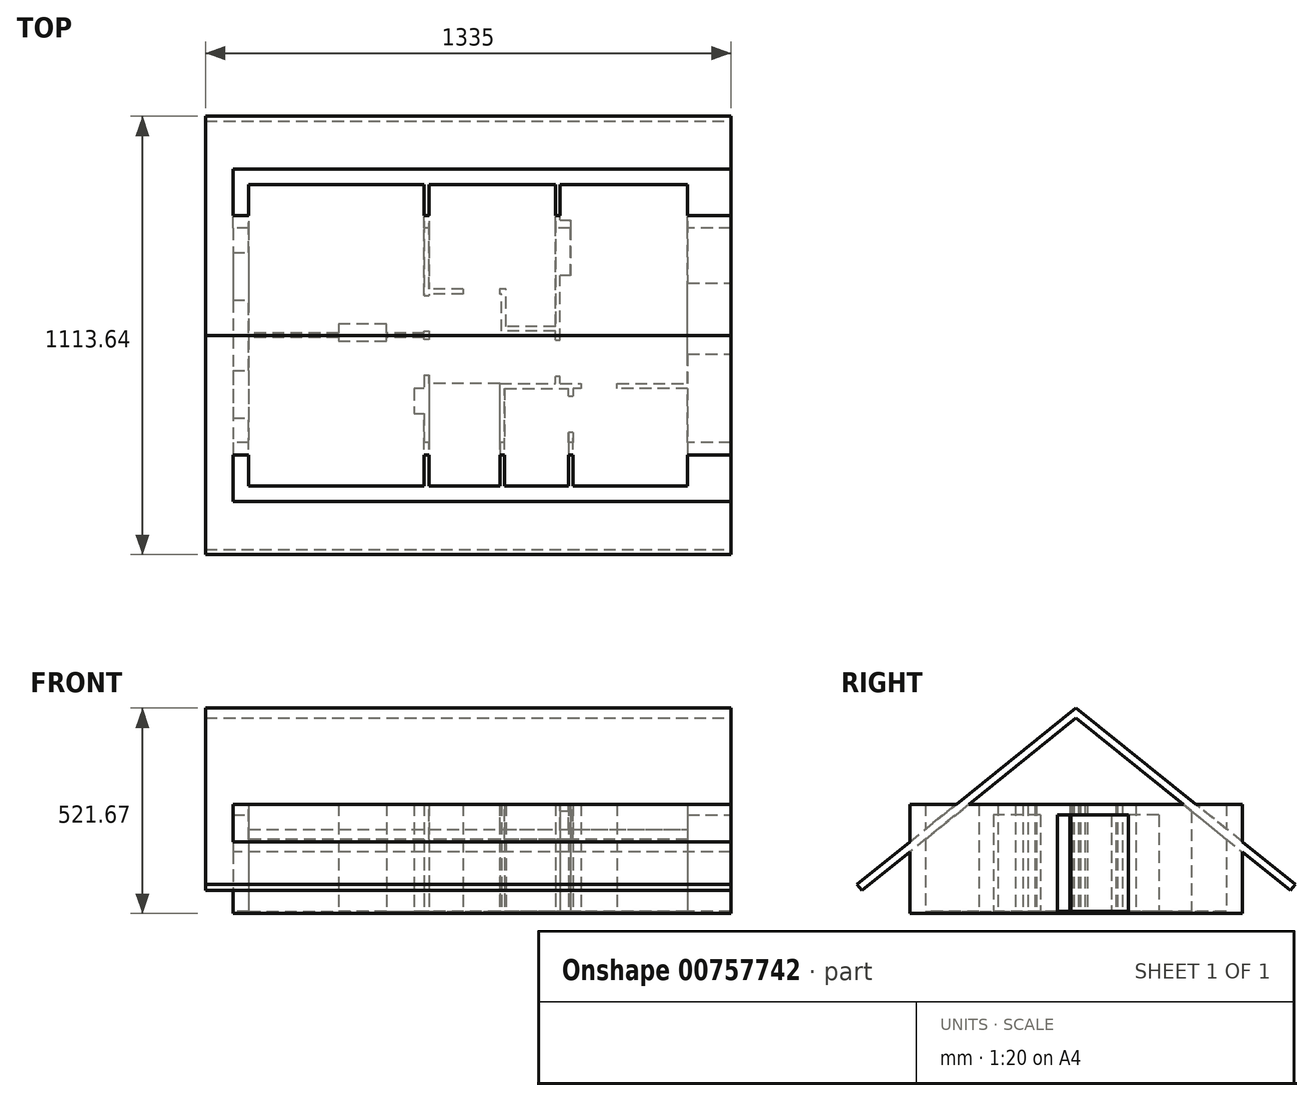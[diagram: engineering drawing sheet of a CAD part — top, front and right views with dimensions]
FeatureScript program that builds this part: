
annotation { "Feature Type Name" : "Feature", "Feature Type Description" : "" }
export const myFeature = defineFeature(function(context is Context, id is Id, definition is map)
    precondition{}
    {
        {
            var Q0;
            Q0=qCreatedBy(makeId("Top.planeOp"),FACE);
            var sketch = newSketch(context, id + "F0", { "sketchPlane" : qUnion([Q0])});
            skLineSegment(sketch, "E0", {"start": v(0, 0) * mm, "end": v(1145, 0) * mm, "construction": true});
            skLineSegment(sketch, "E1", {"start": v(1145, 0) * mm, "end": v(1145, 795) * mm, "construction": true});
            skLineSegment(sketch, "E2", {"start": v(1145, 795) * mm, "end": v(0, 795) * mm, "construction": true});
            skLineSegment(sketch, "E3", {"start": v(0, 795) * mm, "end": v(0, 0) * mm, "construction": true});
            skLineSegment(sketch, "E4", {"start": v(800, 0) * mm, "end": v(800, 15) * mm, "construction": true});
            skLineSegment(sketch, "E5", {"start": v(800, 397.5) * mm, "end": v(0, 397.5) * mm, "construction": true});
            skLineSegment(sketch, "E6.0", {"start": v(1170, 820) * mm, "end": v(-25, 820) * mm});
            skLineSegment(sketch, "E6.1", {"start": v(1170, -25) * mm, "end": v(1170, 820) * mm});
            skLineSegment(sketch, "E6.2", {"start": v(-25, -25) * mm, "end": v(1170, -25) * mm});
            skLineSegment(sketch, "E6.3", {"start": v(-25, 820) * mm, "end": v(-25, -25) * mm});
            skLineSegment(sketch, "E7.0", {"start": v(1130, 780) * mm, "end": v(15, 780) * mm});
            skLineSegment(sketch, "E7.1", {"start": v(1130, 15) * mm, "end": v(1130, 780) * mm});
            skLineSegment(sketch, "E7.2", {"start": v(15, 15) * mm, "end": v(1130, 15) * mm});
            skLineSegment(sketch, "E7.3", {"start": v(15, 780) * mm, "end": v(15, 15) * mm});
            skLineSegment(sketch, "E8.0", {"start": v(806, 263) * mm, "end": v(806, 795) * mm});
            skLineSegment(sketch, "E9.0", {"start": v(794, 263) * mm, "end": v(794, 795) * mm});
            skLineSegment(sketch, "E10", {"start": v(461, 386.5) * mm, "end": v(461, 262.5) * mm});
            skLineSegment(sketch, "E11", {"start": v(461, 262.5) * mm, "end": v(435, 262.5) * mm});
            skLineSegment(sketch, "E12", {"start": v(435, 262.5) * mm, "end": v(435, 198.5) * mm});
            skLineSegment(sketch, "E13", {"start": v(435, 198.5) * mm, "end": v(461, 198.5) * mm});
            skLineSegment(sketch, "E14", {"start": v(461, 198.5) * mm, "end": v(461, 15) * mm});
            skLineSegment(sketch, "E15", {"start": v(806, 691) * mm, "end": v(832, 691) * mm});
            skLineSegment(sketch, "E16", {"start": v(832, 691) * mm, "end": v(832, 549) * mm});
            skLineSegment(sketch, "E17", {"start": v(832, 549) * mm, "end": v(806, 549) * mm});
            skLineSegment(sketch, "E18", {"start": v(365, 426.5) * mm, "end": v(243, 426.5) * mm});
            skLineSegment(sketch, "E19", {"start": v(323, 15) * mm, "end": v(323, -25) * mm});
            skLineSegment(sketch, "E20", {"start": v(461, 15) * mm, "end": v(461, -25) * mm});
            skLineSegment(sketch, "E21", {"start": v(1130, 530) * mm, "end": v(1170, 530) * mm});
            skLineSegment(sketch, "E22", {"start": v(1130, 350) * mm, "end": v(1170, 350) * mm});
            skPoint(sketch, "E23.orphan", {"position": v(238, -25) * mm});
            skPoint(sketch, "E24.end.orphan", {"position": v(88, -25) * mm});
            skLineSegment(sketch, "E25", {"start": v(-25, 487.5) * mm, "end": v(15, 487.5) * mm});
            skLineSegment(sketch, "E26", {"start": v(-25, 607.5) * mm, "end": v(15, 607.5) * mm});
            skLineSegment(sketch, "E27", {"start": v(-25, 307.5) * mm, "end": v(15, 307.5) * mm});
            skLineSegment(sketch, "E28", {"start": v(-25, 187.5) * mm, "end": v(15, 187.5) * mm});
            skLineSegment(sketch, "E29", {"start": v(794, 408) * mm, "end": v(657, 408) * mm});
            skLineSegment(sketch, "E30", {"start": v(657, 408) * mm, "end": v(657, 503) * mm});
            skLineSegment(sketch, "E31", {"start": v(657, 503) * mm, "end": v(473, 503) * mm});
            skLineSegment(sketch, "E32.0", {"start": v(669, 515) * mm, "end": v(473, 515) * mm});
            skLineSegment(sketch, "E32.1", {"start": v(669, 420) * mm, "end": v(669, 515) * mm});
            skLineSegment(sketch, "E32.2", {"start": v(794, 420) * mm, "end": v(669, 420) * mm});
            skLineSegment(sketch, "E33", {"start": v(652, 515) * mm, "end": v(652, 503) * mm});
            skLineSegment(sketch, "E34", {"start": v(560, 515) * mm, "end": v(560, 503) * mm});
            skLineSegment(sketch, "E35", {"start": v(461, 403.5) * mm, "end": v(365, 403.5) * mm});
            skLineSegment(sketch, "E36", {"start": v(365, 403.5) * mm, "end": v(15, 403.5) * mm});
            skLineSegment(sketch, "E37", {"start": v(15, 403.5) * mm, "end": v(15, 382.16) * mm});
            skLineSegment(sketch, "E38", {"start": v(794, 385) * mm, "end": v(806, 385) * mm});
            skLineSegment(sketch, "E39", {"start": v(806, 385) * mm, "end": v(806, 293) * mm});
            skLineSegment(sketch, "E40", {"start": v(806, 293) * mm, "end": v(794, 293) * mm});
            skLineSegment(sketch, "E41.MirrorCS", {"start": v(461, 391.5) * mm, "end": v(365, 391.5) * mm});
            skLineSegment(sketch, "E42.MirrorCS", {"start": v(365, 391.5) * mm, "end": v(15, 391.5) * mm});
            skLineSegment(sketch, "E43", {"start": v(461, 403.5) * mm, "end": v(461, 408.5) * mm});
            skLineSegment(sketch, "E44", {"start": v(461, 408.5) * mm, "end": v(473, 408.5) * mm});
            skLineSegment(sketch, "E45", {"start": v(473, 408.5) * mm, "end": v(473, 386.5) * mm});
            skLineSegment(sketch, "E46", {"start": v(473, 386.5) * mm, "end": v(461, 386.5) * mm});
            skLineSegment(sketch, "E47", {"start": v(461, 386.5) * mm, "end": v(461, 391.5) * mm});
            skLineSegment(sketch, "E48", {"start": v(243, 426.5) * mm, "end": v(243, 382.5) * mm});
            skLineSegment(sketch, "E49", {"start": v(243, 382.5) * mm, "end": v(364.87, 382.5) * mm});
            skLineSegment(sketch, "E50", {"start": v(364.87, 382.5) * mm, "end": v(365, 426.5) * mm});
            skLineSegment(sketch, "E51", {"start": v(461, 408.5) * mm, "end": v(461, 780) * mm});
            skLineSegment(sketch, "E52", {"start": v(461, 780) * mm, "end": v(473, 780) * mm});
            skLineSegment(sketch, "E53", {"start": v(473, 780) * mm, "end": v(473, 408.5) * mm});
            skLineSegment(sketch, "E54", {"start": v(461, 498.5) * mm, "end": v(473, 498.5) * mm});
            skLineSegment(sketch, "E55", {"start": v(473, 386.5) * mm, "end": v(473, 15) * mm});
            skLineSegment(sketch, "E56", {"start": v(461, 296.5) * mm, "end": v(473, 296.5) * mm});
            skLineSegment(sketch, "E57", {"start": v(653, 15) * mm, "end": v(653, 275) * mm});
            skLineSegment(sketch, "E58", {"start": v(653, 275) * mm, "end": v(670, 275) * mm});
            skLineSegment(sketch, "E59", {"start": v(665, 263) * mm, "end": v(665, 15) * mm});
            skLineSegment(sketch, "E60", {"start": v(653, 275) * mm, "end": v(473, 275) * mm});
            skLineSegment(sketch, "E61", {"start": v(670, 275) * mm, "end": v(794, 275) * mm});
            skLineSegment(sketch, "E62", {"start": v(794, 275) * mm, "end": v(794, 263) * mm});
            skLineSegment(sketch, "E63", {"start": v(665, 263) * mm, "end": v(794, 263) * mm});
            skLineSegment(sketch, "E64", {"start": v(794, 275) * mm, "end": v(839, 275) * mm});
            skLineSegment(sketch, "E65", {"start": v(839, 275) * mm, "end": v(839, 15) * mm});
            skLineSegment(sketch, "E66", {"start": v(839, 15) * mm, "end": v(827, 15) * mm});
            skLineSegment(sketch, "E67", {"start": v(827, 15) * mm, "end": v(827, 263) * mm});
            skLineSegment(sketch, "E68", {"start": v(827, 263) * mm, "end": v(794, 263) * mm});
            skLineSegment(sketch, "E69", {"start": v(839, 275) * mm, "end": v(1130, 275) * mm});
            skLineSegment(sketch, "E70", {"start": v(1130, 275) * mm, "end": v(1130, 263) * mm});
            skLineSegment(sketch, "E71", {"start": v(1130, 263) * mm, "end": v(827, 263) * mm});
            skLineSegment(sketch, "E72.trimOffspring", {"start": v(800, 263) * mm, "end": v(800, 795) * mm, "construction": true});
            skLineSegment(sketch, "E73", {"start": v(827, 243) * mm, "end": v(839, 243) * mm});
            skLineSegment(sketch, "E74", {"start": v(839, 243) * mm, "end": v(839, 151) * mm});
            skLineSegment(sketch, "E75", {"start": v(839, 151) * mm, "end": v(827, 151) * mm});
            skLineSegment(sketch, "E76", {"start": v(859, 275) * mm, "end": v(859, 263) * mm});
            skLineSegment(sketch, "E77", {"start": v(859, 263) * mm, "end": v(951, 263) * mm});
            skLineSegment(sketch, "E78", {"start": v(951, 263) * mm, "end": v(951, 275) * mm});
            skSolve(sketch);
        }
        {
            var Q0;
            {var subQ5=sQuery(id+"F0.wireOp",EDGE,"E78");Q0=makeQuery(id+"F0.imprint","IMPRINT",FACE,{"disambiguationData":[TD([[makeQuery(id+"F0.imprint","IMPRINT",EDGE,{"derivedFrom":subQ5}),-1.0]])]});}
            var Q1;
            {var subQ3=sQuery(id+"F0.wireOp",EDGE,"E29");Q1=makeQuery(id+"F0.imprint","IMPRINT",FACE,{"disambiguationData":[TD([[makeQuery(id+"F0.imprint","IMPRINT",EDGE,{"derivedFrom":subQ3}),-1.0]])]});}
            var Q2;
            {var subQ2=sQuery(id+"F0.wireOp",EDGE,"E19");Q2=makeQuery(id+"F0.imprint","IMPRINT",FACE,{"disambiguationData":[TD([[makeQuery(id+"F0.imprint","IMPRINT",EDGE,{"derivedFrom":subQ2}),1.0]])]});}
            var Q3;
            {var subQ0=sQuery(id+"F0.wireOp",EDGE,"E15");Q3=makeQuery(id+"F0.imprint","IMPRINT",FACE,{"disambiguationData":[TD([[makeQuery(id+"F0.imprint","IMPRINT",EDGE,{"derivedFrom":subQ0}),1.0]])]});}
            var Q4;
            {var subQ0=sQuery(id+"F0.wireOp",EDGE,"E25");Q4=makeQuery(id+"F0.imprint","IMPRINT",FACE,{"disambiguationData":[TD([[makeQuery(id+"F0.imprint","IMPRINT",EDGE,{"derivedFrom":subQ0}),1.0]])]});}
            var Q5;
            {var subQ0=sQuery(id+"F0.wireOp",EDGE,"E27");Q5=makeQuery(id+"F0.imprint","IMPRINT",FACE,{"disambiguationData":[TD([[makeQuery(id+"F0.imprint","IMPRINT",EDGE,{"derivedFrom":subQ0}),-1.0]])]});}
            var Q6;
            {var subQ5=sQuery(id+"F0.wireOp",EDGE,"E25");Q6=makeQuery(id+"F0.imprint","IMPRINT",FACE,{"disambiguationData":[TD([[makeQuery(id+"F0.imprint","IMPRINT",EDGE,{"derivedFrom":subQ5}),-1.0]])]});}
            var Q7;
            {var subQ4=sQuery(id+"F0.wireOp",EDGE,"E19");Q7=makeQuery(id+"F0.imprint","IMPRINT",FACE,{"disambiguationData":[TD([[makeQuery(id+"F0.imprint","IMPRINT",EDGE,{"derivedFrom":subQ4}),-1.0]])]});}
            var Q8;
            {var subQ4=sQuery(id+"F0.wireOp",EDGE,"E7.1");var subQ7=sQuery(id+"F0.wireOp",EDGE,"E71");var subQ8=makeQuery(id+"F0.imprint","INTERSECT",VERTEX,{"derivedFrom":[subQ4,subQ7]});Q8=makeQuery(id+"F0.imprint","IMPRINT",FACE,{"disambiguationData":[TD([[makeQuery(id+"F0.imprint","IMPRINT",EDGE,{"disambiguationData":[TD([[subQ8,1.0]])],"derivedFrom":subQ4}),1.0]])]});}
            var Q9;
            {var subQ2=sQuery(id+"F0.wireOp",EDGE,"E76");Q9=makeQuery(id+"F0.imprint","IMPRINT",FACE,{"disambiguationData":[TD([[makeQuery(id+"F0.imprint","IMPRINT",EDGE,{"derivedFrom":subQ2}),1.0]])]});}
            var Q10;
            {var subQ5=sQuery(id+"F0.wireOp",EDGE,"E49");Q10=makeQuery(id+"F0.imprint","IMPRINT",FACE,{"disambiguationData":[TD([[makeQuery(id+"F0.imprint","IMPRINT",EDGE,{"derivedFrom":subQ5}),1.0]])]});}
            var Q11;
            {var subQ6=sQuery(id+"F0.wireOp",EDGE,"E54");Q11=makeQuery(id+"F0.imprint","IMPRINT",FACE,{"disambiguationData":[TD([[makeQuery(id+"F0.imprint","IMPRINT",EDGE,{"derivedFrom":subQ6}),1.0]])]});}
            var Q12;
            {var subQ0=sQuery(id+"F0.wireOp",EDGE,"E44");Q12=makeQuery(id+"F0.imprint","IMPRINT",FACE,{"disambiguationData":[TD([[makeQuery(id+"F0.imprint","IMPRINT",EDGE,{"derivedFrom":subQ0}),1.0]])]});}
            var Q13;
            {var subQ0=sQuery(id+"F0.wireOp",EDGE,"E18");Q13=makeQuery(id+"F0.imprint","IMPRINT",FACE,{"disambiguationData":[TD([[makeQuery(id+"F0.imprint","IMPRINT",EDGE,{"derivedFrom":subQ0}),1.0]])]});}
            var Q14;
            {var subQ9=sQuery(id+"F0.wireOp",EDGE,"E29");Q14=makeQuery(id+"F0.imprint","IMPRINT",FACE,{"disambiguationData":[TD([[makeQuery(id+"F0.imprint","IMPRINT",EDGE,{"derivedFrom":subQ9}),1.0]])]});}
            var Q15;
            {var subQ0=sQuery(id+"F0.wireOp",EDGE,"E21");Q15=makeQuery(id+"F0.imprint","IMPRINT",FACE,{"disambiguationData":[TD([[makeQuery(id+"F0.imprint","IMPRINT",EDGE,{"derivedFrom":subQ0}),-1.0]])]});}
            var Q16;
            {var subQ7=sQuery(id+"F0.wireOp",EDGE,"E59");Q16=makeQuery(id+"F0.imprint","IMPRINT",FACE,{"disambiguationData":[TD([[makeQuery(id+"F0.imprint","IMPRINT",EDGE,{"derivedFrom":subQ7}),1.0]])]});}
            var Q17;
            {var subQ0=sQuery(id+"F0.wireOp",EDGE,"E34");Q17=makeQuery(id+"F0.imprint","IMPRINT",FACE,{"disambiguationData":[TD([[makeQuery(id+"F0.imprint","IMPRINT",EDGE,{"derivedFrom":subQ0}),-1.0]])]});}
            var Q18;
            {var subQ0=sQuery(id+"F0.wireOp",EDGE,"E46");Q18=makeQuery(id+"F0.imprint","IMPRINT",FACE,{"disambiguationData":[TD([[makeQuery(id+"F0.imprint","IMPRINT",EDGE,{"derivedFrom":subQ0}),1.0]])]});}
            var Q19;
            {var subQ0=sQuery(id+"F0.wireOp",EDGE,"E11");Q19=makeQuery(id+"F0.imprint","IMPRINT",FACE,{"disambiguationData":[TD([[makeQuery(id+"F0.imprint","IMPRINT",EDGE,{"derivedFrom":subQ0}),-1.0]])]});}
            var Q20;
            {var subQ5=sQuery(id+"F0.wireOp",EDGE,"E6.0");Q20=makeQuery(id+"F0.imprint","IMPRINT",FACE,{"disambiguationData":[TD([[makeQuery(id+"F0.imprint","IMPRINT",EDGE,{"derivedFrom":subQ5}),1.0]])]});}
            var Q21;
            {var subQ2=sQuery(id+"F0.wireOp",EDGE,"E73");Q21=makeQuery(id+"F0.imprint","IMPRINT",FACE,{"disambiguationData":[TD([[makeQuery(id+"F0.imprint","IMPRINT",EDGE,{"derivedFrom":subQ2}),-1.0]])]});}
            var Q22;
            {var subQ0=sQuery(id+"F0.wireOp",EDGE,"E11");Q22=makeQuery(id+"F0.imprint","IMPRINT",FACE,{"disambiguationData":[TD([[makeQuery(id+"F0.imprint","IMPRINT",EDGE,{"derivedFrom":subQ0}),1.0]])]});}
            var Q23;
            {var subQ10=sQuery(id+"F0.wireOp",EDGE,"E32.1");Q23=makeQuery(id+"F0.imprint","IMPRINT",FACE,{"disambiguationData":[TD([[makeQuery(id+"F0.imprint","IMPRINT",EDGE,{"derivedFrom":subQ10}),-1.0]])]});}
            var Q24;
            {var subQ0=sQuery(id+"F0.wireOp",EDGE,"E15");Q24=makeQuery(id+"F0.imprint","IMPRINT",FACE,{"disambiguationData":[TD([[makeQuery(id+"F0.imprint","IMPRINT",EDGE,{"derivedFrom":subQ0}),-1.0]])]});}
            var Q25;
            {var subQ0=sQuery(id+"F0.wireOp",EDGE,"E33");Q25=makeQuery(id+"F0.imprint","IMPRINT",FACE,{"disambiguationData":[TD([[makeQuery(id+"F0.imprint","IMPRINT",EDGE,{"derivedFrom":subQ0}),-1.0]])]});}
            var Q26;
            {var subQ5=sQuery(id+"F0.wireOp",EDGE,"E75");Q26=makeQuery(id+"F0.imprint","IMPRINT",FACE,{"disambiguationData":[TD([[makeQuery(id+"F0.imprint","IMPRINT",EDGE,{"derivedFrom":subQ5}),1.0]])]});}
            var Q27;
            {var subQ3=sQuery(id+"F0.wireOp",EDGE,"E57");Q27=makeQuery(id+"F0.imprint","IMPRINT",FACE,{"disambiguationData":[TD([[makeQuery(id+"F0.imprint","IMPRINT",EDGE,{"derivedFrom":subQ3}),-1.0]])]});}
            var Q28;
            {var subQ8=sQuery(id+"F0.wireOp",EDGE,"E20");Q28=makeQuery(id+"F0.imprint","IMPRINT",FACE,{"disambiguationData":[TD([[makeQuery(id+"F0.imprint","IMPRINT",EDGE,{"derivedFrom":subQ8}),1.0]])]});}
            var Q29;
            {var subQ0=sQuery(id+"F0.wireOp",EDGE,"E38");Q29=makeQuery(id+"F0.imprint","IMPRINT",FACE,{"disambiguationData":[TD([[makeQuery(id+"F0.imprint","IMPRINT",EDGE,{"derivedFrom":subQ0}),-1.0]])]});}
            var Q30;
            {var subQ0=sQuery(id+"F0.wireOp",EDGE,"E36");var subQ1=sQuery(id+"F0.wireOp",EDGE,"E7.3");var subQ2=makeQuery(id+"F0.imprint","INTERSECT",VERTEX,{"derivedFrom":[subQ1,subQ0]});Q30=makeQuery(id+"F0.imprint","IMPRINT",FACE,{"disambiguationData":[TD([[makeQuery(id+"F0.imprint","IMPRINT",EDGE,{"disambiguationData":[TD([[subQ2,-1.0]])],"derivedFrom":subQ1}),1.0]])]});}
            var Q31;
            {var subQ3=sQuery(id+"F0.wireOp",EDGE,"E40");Q31=makeQuery(id+"F0.imprint","IMPRINT",FACE,{"disambiguationData":[TD([[makeQuery(id+"F0.imprint","IMPRINT",EDGE,{"derivedFrom":subQ3}),1.0]])]});}
            var Q32;
            {var subQ5=sQuery(id+"F0.wireOp",EDGE,"E38");Q32=makeQuery(id+"F0.imprint","IMPRINT",FACE,{"disambiguationData":[TD([[makeQuery(id+"F0.imprint","IMPRINT",EDGE,{"derivedFrom":subQ5}),1.0]])]});}
            var Q33;
            {var subQ3=sQuery(id+"F0.wireOp",EDGE,"E73");Q33=makeQuery(id+"F0.imprint","IMPRINT",FACE,{"disambiguationData":[TD([[makeQuery(id+"F0.imprint","IMPRINT",EDGE,{"derivedFrom":subQ3}),1.0]])]});}
            var Q34;
            {var subQ3=sQuery(id+"F0.wireOp",EDGE,"E64");var subQ5=sQuery(id+"F0.wireOp",EDGE,"E8.0");var subQ6=makeQuery(id+"F0.imprint","INTERSECT",VERTEX,{"derivedFrom":[subQ5,subQ3]});Q34=makeQuery(id+"F0.imprint","IMPRINT",FACE,{"disambiguationData":[TD([[makeQuery(id+"F0.imprint","IMPRINT",EDGE,{"disambiguationData":[TD([[subQ6,1.0]])],"derivedFrom":subQ5}),-1.0]])]});}
            var Q35;
            {var subQ5=sQuery(id+"F0.wireOp",EDGE,"E76");Q35=makeQuery(id+"F0.imprint","IMPRINT",FACE,{"disambiguationData":[TD([[makeQuery(id+"F0.imprint","IMPRINT",EDGE,{"derivedFrom":subQ5}),-1.0]])]});}
            var Q36;
            {var subQ6=sQuery(id+"F0.wireOp",EDGE,"E35");Q36=makeQuery(id+"F0.imprint","IMPRINT",FACE,{"disambiguationData":[TD([[makeQuery(id+"F0.imprint","IMPRINT",EDGE,{"derivedFrom":subQ6}),1.0]])]});}
            var Q37;
            {var subQ0=sQuery(id+"F0.wireOp",EDGE,"E48");var subQ1=sQuery(id+"F0.wireOp",EDGE,"E36");var subQ2=makeQuery(id+"F0.imprint","INTERSECT",VERTEX,{"derivedFrom":[subQ1,subQ0]});Q37=makeQuery(id+"F0.imprint","IMPRINT",FACE,{"disambiguationData":[TD([[makeQuery(id+"F0.imprint","IMPRINT",EDGE,{"disambiguationData":[TD([[subQ2,1.0]])],"derivedFrom":subQ1}),1.0]])]});}
            var Q38;
            {var subQ0=sQuery(id+"F0.wireOp",EDGE,"E64");var subQ1=sQuery(id+"F0.wireOp",EDGE,"E8.0");var subQ2=makeQuery(id+"F0.imprint","INTERSECT",VERTEX,{"derivedFrom":[subQ1,subQ0]});Q38=makeQuery(id+"F0.imprint","IMPRINT",FACE,{"disambiguationData":[TD([[makeQuery(id+"F0.imprint","IMPRINT",EDGE,{"disambiguationData":[TD([[subQ2,1.0]])],"derivedFrom":subQ1}),1.0]])]});}
            var Q39;
            {var subQ1=sQuery(id+"F0.wireOp",EDGE,"E18");Q39=makeQuery(id+"F0.imprint","IMPRINT",FACE,{"disambiguationData":[TD([[makeQuery(id+"F0.imprint","IMPRINT",EDGE,{"derivedFrom":subQ1}),-1.0]])]});}
            extrude(context, id + "F1", {"entities" : qUnion([Q0, Q1, Q2, Q3, Q4, Q5, Q6, Q7, Q8, Q9, Q10, Q11, Q12, Q13, Q14, Q15, Q16, Q17, Q18, Q19, Q20, Q21, Q22, Q23, Q24, Q25, Q26, Q27, Q28, Q29, Q30, Q31, Q32, Q33, Q34, Q35, Q36, Q37, Q38, Q39]), "depth" : 5 * mm, "offsetDistance" : 25 * mm});
        }
        {
            var Q0;
            {var subQ4=sQuery(id+"F0.wireOp",EDGE,"E19");Q0=makeQuery(id+"F0.imprint","IMPRINT",FACE,{"disambiguationData":[TD([[makeQuery(id+"F0.imprint","IMPRINT",EDGE,{"derivedFrom":subQ4}),-1.0]])]});}
            var Q1;
            {var subQ2=sQuery(id+"F0.wireOp",EDGE,"E19");Q1=makeQuery(id+"F0.imprint","IMPRINT",FACE,{"disambiguationData":[TD([[makeQuery(id+"F0.imprint","IMPRINT",EDGE,{"derivedFrom":subQ2}),1.0]])]});}
            var Q2;
            {var subQ8=sQuery(id+"F0.wireOp",EDGE,"E20");Q2=makeQuery(id+"F0.imprint","IMPRINT",FACE,{"disambiguationData":[TD([[makeQuery(id+"F0.imprint","IMPRINT",EDGE,{"derivedFrom":subQ8}),1.0]])]});}
            var Q3;
            {var subQ5=sQuery(id+"F0.wireOp",EDGE,"E75");Q3=makeQuery(id+"F0.imprint","IMPRINT",FACE,{"disambiguationData":[TD([[makeQuery(id+"F0.imprint","IMPRINT",EDGE,{"derivedFrom":subQ5}),1.0]])]});}
            var Q4;
            {var subQ3=sQuery(id+"F0.wireOp",EDGE,"E57");Q4=makeQuery(id+"F0.imprint","IMPRINT",FACE,{"disambiguationData":[TD([[makeQuery(id+"F0.imprint","IMPRINT",EDGE,{"derivedFrom":subQ3}),-1.0]])]});}
            var Q5;
            {var subQ0=sQuery(id+"F0.wireOp",EDGE,"E11");Q5=makeQuery(id+"F0.imprint","IMPRINT",FACE,{"disambiguationData":[TD([[makeQuery(id+"F0.imprint","IMPRINT",EDGE,{"derivedFrom":subQ0}),1.0]])]});}
            var Q6;
            {var subQ5=sQuery(id+"F0.wireOp",EDGE,"E25");Q6=makeQuery(id+"F0.imprint","IMPRINT",FACE,{"disambiguationData":[TD([[makeQuery(id+"F0.imprint","IMPRINT",EDGE,{"derivedFrom":subQ5}),-1.0]])]});}
            var Q7;
            {var subQ0=sQuery(id+"F0.wireOp",EDGE,"E36");var subQ1=sQuery(id+"F0.wireOp",EDGE,"E7.3");var subQ2=makeQuery(id+"F0.imprint","INTERSECT",VERTEX,{"derivedFrom":[subQ1,subQ0]});Q7=makeQuery(id+"F0.imprint","IMPRINT",FACE,{"disambiguationData":[TD([[makeQuery(id+"F0.imprint","IMPRINT",EDGE,{"disambiguationData":[TD([[subQ2,-1.0]])],"derivedFrom":subQ1}),1.0]])]});}
            var Q8;
            {var subQ0=sQuery(id+"F0.wireOp",EDGE,"E18");Q8=makeQuery(id+"F0.imprint","IMPRINT",FACE,{"disambiguationData":[TD([[makeQuery(id+"F0.imprint","IMPRINT",EDGE,{"derivedFrom":subQ0}),1.0]])]});}
            var Q9;
            {var subQ0=sQuery(id+"F0.wireOp",EDGE,"E48");var subQ1=sQuery(id+"F0.wireOp",EDGE,"E36");var subQ2=makeQuery(id+"F0.imprint","INTERSECT",VERTEX,{"derivedFrom":[subQ1,subQ0]});Q9=makeQuery(id+"F0.imprint","IMPRINT",FACE,{"disambiguationData":[TD([[makeQuery(id+"F0.imprint","IMPRINT",EDGE,{"disambiguationData":[TD([[subQ2,1.0]])],"derivedFrom":subQ1}),1.0]])]});}
            var Q10;
            {var subQ5=sQuery(id+"F0.wireOp",EDGE,"E49");Q10=makeQuery(id+"F0.imprint","IMPRINT",FACE,{"disambiguationData":[TD([[makeQuery(id+"F0.imprint","IMPRINT",EDGE,{"derivedFrom":subQ5}),1.0]])]});}
            var Q11;
            {var subQ6=sQuery(id+"F0.wireOp",EDGE,"E35");Q11=makeQuery(id+"F0.imprint","IMPRINT",FACE,{"disambiguationData":[TD([[makeQuery(id+"F0.imprint","IMPRINT",EDGE,{"derivedFrom":subQ6}),1.0]])]});}
            var Q12;
            {var subQ6=sQuery(id+"F0.wireOp",EDGE,"E54");Q12=makeQuery(id+"F0.imprint","IMPRINT",FACE,{"disambiguationData":[TD([[makeQuery(id+"F0.imprint","IMPRINT",EDGE,{"derivedFrom":subQ6}),1.0]])]});}
            var Q13;
            {var subQ0=sQuery(id+"F0.wireOp",EDGE,"E34");Q13=makeQuery(id+"F0.imprint","IMPRINT",FACE,{"disambiguationData":[TD([[makeQuery(id+"F0.imprint","IMPRINT",EDGE,{"derivedFrom":subQ0}),-1.0]])]});}
            var Q14;
            {var subQ3=sQuery(id+"F0.wireOp",EDGE,"E29");Q14=makeQuery(id+"F0.imprint","IMPRINT",FACE,{"disambiguationData":[TD([[makeQuery(id+"F0.imprint","IMPRINT",EDGE,{"derivedFrom":subQ3}),-1.0]])]});}
            var Q15;
            {var subQ5=sQuery(id+"F0.wireOp",EDGE,"E38");Q15=makeQuery(id+"F0.imprint","IMPRINT",FACE,{"disambiguationData":[TD([[makeQuery(id+"F0.imprint","IMPRINT",EDGE,{"derivedFrom":subQ5}),1.0]])]});}
            var Q16;
            {var subQ3=sQuery(id+"F0.wireOp",EDGE,"E73");Q16=makeQuery(id+"F0.imprint","IMPRINT",FACE,{"disambiguationData":[TD([[makeQuery(id+"F0.imprint","IMPRINT",EDGE,{"derivedFrom":subQ3}),1.0]])]});}
            var Q17;
            {var subQ5=sQuery(id+"F0.wireOp",EDGE,"E76");Q17=makeQuery(id+"F0.imprint","IMPRINT",FACE,{"disambiguationData":[TD([[makeQuery(id+"F0.imprint","IMPRINT",EDGE,{"derivedFrom":subQ5}),-1.0]])]});}
            var Q18;
            {var subQ3=sQuery(id+"F0.wireOp",EDGE,"E64");var subQ5=sQuery(id+"F0.wireOp",EDGE,"E8.0");var subQ6=makeQuery(id+"F0.imprint","INTERSECT",VERTEX,{"derivedFrom":[subQ5,subQ3]});Q18=makeQuery(id+"F0.imprint","IMPRINT",FACE,{"disambiguationData":[TD([[makeQuery(id+"F0.imprint","IMPRINT",EDGE,{"disambiguationData":[TD([[subQ6,1.0]])],"derivedFrom":subQ5}),-1.0]])]});}
            var Q19;
            {var subQ0=sQuery(id+"F0.wireOp",EDGE,"E64");var subQ1=sQuery(id+"F0.wireOp",EDGE,"E8.0");var subQ2=makeQuery(id+"F0.imprint","INTERSECT",VERTEX,{"derivedFrom":[subQ1,subQ0]});Q19=makeQuery(id+"F0.imprint","IMPRINT",FACE,{"disambiguationData":[TD([[makeQuery(id+"F0.imprint","IMPRINT",EDGE,{"disambiguationData":[TD([[subQ2,1.0]])],"derivedFrom":subQ1}),1.0]])]});}
            var Q20;
            {var subQ3=sQuery(id+"F0.wireOp",EDGE,"E40");Q20=makeQuery(id+"F0.imprint","IMPRINT",FACE,{"disambiguationData":[TD([[makeQuery(id+"F0.imprint","IMPRINT",EDGE,{"derivedFrom":subQ3}),1.0]])]});}
            var Q21;
            {var subQ5=sQuery(id+"F0.wireOp",EDGE,"E78");Q21=makeQuery(id+"F0.imprint","IMPRINT",FACE,{"disambiguationData":[TD([[makeQuery(id+"F0.imprint","IMPRINT",EDGE,{"derivedFrom":subQ5}),-1.0]])]});}
            var Q22;
            {var subQ5=sQuery(id+"F0.wireOp",EDGE,"E6.0");Q22=makeQuery(id+"F0.imprint","IMPRINT",FACE,{"disambiguationData":[TD([[makeQuery(id+"F0.imprint","IMPRINT",EDGE,{"derivedFrom":subQ5}),1.0]])]});}
            var Q23;
            {var subQ0=sQuery(id+"F0.wireOp",EDGE,"E15");Q23=makeQuery(id+"F0.imprint","IMPRINT",FACE,{"disambiguationData":[TD([[makeQuery(id+"F0.imprint","IMPRINT",EDGE,{"derivedFrom":subQ0}),-1.0]])]});}
            extrude(context, id + "F2", {"entities" : qUnion([Q0, Q1, Q2, Q3, Q4, Q5, Q6, Q7, Q8, Q9, Q10, Q11, Q12, Q13, Q14, Q15, Q16, Q17, Q18, Q19, Q20, Q21, Q22, Q23]), "operationType" : NewBodyOperationType.ADD, "depth" : (549 - 272) * mm, "offsetDistance" : 25 * mm});
        }
        {
            var Q0;
            Q0=makeQuery(id+"F2.opExtrude","CAP_FACE",FACE,{"disambiguationData":[OSD([sQuery(id+"F0.wireOp",EDGE,"E6.0"),sQuery(id+"F0.wireOp",EDGE,"E6.1"),sQuery(id+"F0.wireOp",EDGE,"E6.3"),sQuery(id+"F0.wireOp",EDGE,"E7.0"),sQuery(id+"F0.wireOp",EDGE,"E7.1"),sQuery(id+"F0.wireOp",EDGE,"E7.3"),sQuery(id+"F0.wireOp",EDGE,"E8.0"),sQuery(id+"F0.wireOp",EDGE,"E9.0"),sQuery(id+"F0.wireOp",EDGE,"E15"),sQuery(id+"F0.wireOp",EDGE,"E16"),sQuery(id+"F0.wireOp",EDGE,"E17"),sQuery(id+"F0.wireOp",EDGE,"E21"),sQuery(id+"F0.wireOp",EDGE,"E26"),sQuery(id+"F0.wireOp",EDGE,"E29"),sQuery(id+"F0.wireOp",EDGE,"E30"),sQuery(id+"F0.wireOp",EDGE,"E31"),sQuery(id+"F0.wireOp",EDGE,"E32.0"),sQuery(id+"F0.wireOp",EDGE,"E32.1"),sQuery(id+"F0.wireOp",EDGE,"E32.2"),sQuery(id+"F0.wireOp",EDGE,"E33"),sQuery(id+"F0.wireOp",EDGE,"E34"),sQuery(id+"F0.wireOp",EDGE,"E38"),sQuery(id+"F0.wireOp",EDGE,"E51"),sQuery(id+"F0.wireOp",EDGE,"E53"),sQuery(id+"F0.wireOp",EDGE,"E54")])],"isStart":false});
            var sketch = newSketch(context, id + "F3", { "sketchPlane" : qUnion([Q0])});
            skLineSegment(sketch, "E79.0", {"start": v(15, 780) * mm, "end": v(15, 15) * mm});
            skLineSegment(sketch, "E80.0", {"start": v(-25, 820) * mm, "end": v(-25, -25) * mm});
            skLineSegment(sketch, "E81.0", {"start": v(-25, 487.5) * mm, "end": v(15, 487.5) * mm});
            skLineSegment(sketch, "E82.0", {"start": v(-25, 607.5) * mm, "end": v(15, 607.5) * mm});
            skLineSegment(sketch, "E83.0", {"start": v(-25, 307.5) * mm, "end": v(15, 307.5) * mm});
            skLineSegment(sketch, "E84.0", {"start": v(-25, 187.5) * mm, "end": v(15, 187.5) * mm});
            skLineSegment(sketch, "E85.0", {"start": v(1170, -25) * mm, "end": v(1170, 820) * mm});
            skLineSegment(sketch, "E86.0", {"start": v(1130, 15) * mm, "end": v(1130, 780) * mm});
            skLineSegment(sketch, "E87.0", {"start": v(1130, 530) * mm, "end": v(1170, 530) * mm});
            skLineSegment(sketch, "E88.0", {"start": v(1130, 350) * mm, "end": v(1170, 350) * mm});
            skSolve(sketch);
        }
        {
            var Q0;
            Q0=qSketchRegion(id+"F3",true);
            extrude(context, id + "F4", {"entities" : qUnion([Q0]), "operationType" : NewBodyOperationType.ADD, "oppositeDirection" : true, "depth" : (277 - 250) * mm, "offsetDistance" : 25 * mm});
        }
        {
            var Q0;
            {var subQ0=sQuery(id+"F0.wireOp",EDGE,"E6.3");Q0=makeQuery(id+"F4.boolean.opBoolean","MERGE",FACE,{"derivedFrom":[makeQuery(id+"F2.boolean.opBoolean","MERGE",FACE,{"derivedFrom":[makeQuery(id+"F1.opExtrude","SWEPT_FACE",FACE,{"disambiguationData":[OSD([subQ0])]}),makeQuery(id+"F2.opExtrude","SWEPT_FACE",FACE,{"disambiguationData":[OSD([subQ0]),TDD([makeQuery(id+"F0.imprint","IMPRINT",EDGE,{"disambiguationData":[TD([[makeQuery(id+"F0.imprint","INTERSECT",VERTEX,{"derivedFrom":[sQuery(id+"F0.wireOp",EDGE,"E6.0"),subQ0]}),-1.0]])],"derivedFrom":subQ0})])]}),makeQuery(id+"F2.opExtrude","SWEPT_FACE",FACE,{"disambiguationData":[OSD([subQ0]),TDD([makeQuery(id+"F0.imprint","IMPRINT",EDGE,{"disambiguationData":[TD([[makeQuery(id+"F0.imprint","INTERSECT",VERTEX,{"derivedFrom":[subQ0,sQuery(id+"F0.wireOp",EDGE,"E28")]}),-1.0]])],"derivedFrom":subQ0})])]}),makeQuery(id+"F2.opExtrude","SWEPT_FACE",FACE,{"disambiguationData":[OSD([subQ0]),TDD([makeQuery(id+"F0.imprint","IMPRINT",EDGE,{"disambiguationData":[TD([[makeQuery(id+"F0.imprint","INTERSECT",VERTEX,{"derivedFrom":[subQ0,sQuery(id+"F0.wireOp",EDGE,"E25")]}),-1.0]])],"derivedFrom":subQ0})])]})]}),makeQuery(id+"F4.opExtrude","SWEPT_FACE",FACE,{"disambiguationData":[OSD([sQuery(id+"F3.wireOp",EDGE,"E80.0")])]})]});}
            var sketch = newSketch(context, id + "F5", { "sketchPlane" : qUnion([Q0])});
            skLineSegment(sketch, "E89", {"start": v(-397.5, 277) * mm, "end": v(-397.5, 496) * mm, "construction": true});
            skLineSegment(sketch, "E90", {"start": v(-820, 0) * mm, "end": v(-820, 156) * mm, "construction": true});
            skLineSegment(sketch, "E91", {"start": v(-397.5, 496) * mm, "end": v(-820, 156) * mm});
            skLineSegment(sketch, "E92.MirrorCS", {"start": v(-397.5, 496) * mm, "end": v(25, 156) * mm});
            skLineSegment(sketch, "E93", {"start": v(-820, 156) * mm, "end": v(-820, 496) * mm});
            skLineSegment(sketch, "E94", {"start": v(-820, 496) * mm, "end": v(25, 496) * mm});
            skLineSegment(sketch, "E95", {"start": v(25, 496) * mm, "end": v(25, 156) * mm});
            skLineSegment(sketch, "E96", {"start": v(25, 156) * mm, "end": v(146.78, 58) * mm});
            skLineSegment(sketch, "E97", {"start": v(146.78, 58) * mm, "end": v(159.32, 73.58) * mm});
            skLineSegment(sketch, "E98", {"start": v(159.32, 73.58) * mm, "end": v(-397.5, 521.67) * mm});
            skLineSegment(sketch, "E99.MirrorCS", {"start": v(-954.32, 73.58) * mm, "end": v(-397.5, 521.67) * mm});
            skLineSegment(sketch, "E100.MirrorCS", {"start": v(-820, 156) * mm, "end": v(-941.78, 58) * mm});
            skLineSegment(sketch, "E101.MirrorCS", {"start": v(-941.78, 58) * mm, "end": v(-954.32, 73.58) * mm});
            skSolve(sketch);
        }
        {
            var Q0;
            {var subQ0=sQuery(id+"F5.wireOp",EDGE,"E94");var subQ6=sQuery(id+"F5.wireOp",EDGE,"E98");var subQ7=makeQuery(id+"F5.imprint","INTERSECT",VERTEX,{"derivedFrom":[subQ0,subQ6]});Q0=makeQuery(id+"F5.imprint","IMPRINT",FACE,{"disambiguationData":[TD([[makeQuery(id+"F5.imprint","IMPRINT",EDGE,{"disambiguationData":[TD([[subQ7,1.0]])],"derivedFrom":subQ0}),-1.0]])]});}
            var Q1;
            {var subQ0=sQuery(id+"F5.wireOp",EDGE,"E95");var subQ7=sQuery(id+"F5.wireOp",EDGE,"E98");var subQ8=makeQuery(id+"F5.imprint","INTERSECT",VERTEX,{"derivedFrom":[subQ0,subQ7]});Q1=makeQuery(id+"F5.imprint","IMPRINT",FACE,{"disambiguationData":[TD([[makeQuery(id+"F5.imprint","IMPRINT",EDGE,{"disambiguationData":[TD([[subQ8,-1.0]])],"derivedFrom":subQ0}),-1.0]])]});}
            var Q2;
            {var subQ0=sQuery(id+"F5.wireOp",EDGE,"E96");Q2=makeQuery(id+"F5.imprint","IMPRINT",FACE,{"disambiguationData":[TD([[makeQuery(id+"F5.imprint","IMPRINT",EDGE,{"derivedFrom":subQ0}),1.0]])]});}
            var Q3;
            {var subQ2=sQuery(id+"F5.wireOp",EDGE,"E99.MirrorCS");var subQ4=sQuery(id+"F5.wireOp",EDGE,"E98");var subQ5=makeQuery(id+"F5.imprint","INTERSECT",VERTEX,{"derivedFrom":[subQ4,subQ2]});Q3=makeQuery(id+"F5.imprint","IMPRINT",FACE,{"disambiguationData":[TD([[makeQuery(id+"F5.imprint","IMPRINT",EDGE,{"disambiguationData":[TD([[subQ5,1.0]])],"derivedFrom":subQ4}),1.0]])]});}
            var Q4;
            {var subQ0=sQuery(id+"F5.wireOp",EDGE,"E94");var subQ6=sQuery(id+"F5.wireOp",EDGE,"E99.MirrorCS");var subQ8=makeQuery(id+"F5.imprint","INTERSECT",VERTEX,{"derivedFrom":[subQ0,subQ6]});Q4=makeQuery(id+"F5.imprint","IMPRINT",FACE,{"disambiguationData":[TD([[makeQuery(id+"F5.imprint","IMPRINT",EDGE,{"disambiguationData":[TD([[subQ8,-1.0]])],"derivedFrom":subQ0}),-1.0]])]});}
            var Q5;
            {var subQ0=sQuery(id+"F5.wireOp",EDGE,"E100.MirrorCS");Q5=makeQuery(id+"F5.imprint","IMPRINT",FACE,{"disambiguationData":[TD([[makeQuery(id+"F5.imprint","IMPRINT",EDGE,{"derivedFrom":subQ0}),-1.0]])]});}
            var Q6;
            {var subQ0=sQuery(id+"F5.wireOp",EDGE,"E93");var subQ7=sQuery(id+"F5.wireOp",EDGE,"E99.MirrorCS");var subQ8=makeQuery(id+"F5.imprint","INTERSECT",VERTEX,{"derivedFrom":[subQ0,subQ7]});Q6=makeQuery(id+"F5.imprint","IMPRINT",FACE,{"disambiguationData":[TD([[makeQuery(id+"F5.imprint","IMPRINT",EDGE,{"disambiguationData":[TD([[subQ8,-1.0]])],"derivedFrom":subQ0}),1.0]])]});}
            extrude(context, id + "F6", {"entities" : qUnion([Q0, Q1, Q2, Q3, Q4, Q5, Q6]), "operationType" : NewBodyOperationType.ADD, "depth" : 70 * mm, "offsetDistance" : 25 * mm});
        }
        {
            var Q0;
            Q0=makeQuery(id+"F6.opExtrude","CAP_FACE",FACE,{"disambiguationData":[OSD([sQuery(id+"F5.wireOp",EDGE,"E91"),sQuery(id+"F5.wireOp",EDGE,"E92.MirrorCS"),sQuery(id+"F5.wireOp",EDGE,"E96"),sQuery(id+"F5.wireOp",EDGE,"E97"),sQuery(id+"F5.wireOp",EDGE,"E98"),sQuery(id+"F5.wireOp",EDGE,"E99.MirrorCS"),sQuery(id+"F5.wireOp",EDGE,"E100.MirrorCS"),sQuery(id+"F5.wireOp",EDGE,"E101.MirrorCS")])],"isStart":false});
            var Q1;
            {var subQ0=sQuery(id+"F0.wireOp",EDGE,"E6.1");Q1=makeQuery(id+"F4.boolean.opBoolean","MERGE",FACE,{"derivedFrom":[makeQuery(id+"F2.boolean.opBoolean","MERGE",FACE,{"derivedFrom":[makeQuery(id+"F1.opExtrude","SWEPT_FACE",FACE,{"disambiguationData":[OSD([subQ0])]}),makeQuery(id+"F2.opExtrude","SWEPT_FACE",FACE,{"disambiguationData":[OSD([subQ0]),TDD([makeQuery(id+"F0.imprint","IMPRINT",EDGE,{"disambiguationData":[TD([[makeQuery(id+"F0.imprint","INTERSECT",VERTEX,{"derivedFrom":[subQ0,sQuery(id+"F0.wireOp",EDGE,"E6.2")]}),-1.0]])],"derivedFrom":subQ0})])]}),makeQuery(id+"F2.opExtrude","SWEPT_FACE",FACE,{"disambiguationData":[OSD([subQ0]),TDD([makeQuery(id+"F0.imprint","IMPRINT",EDGE,{"disambiguationData":[TD([[makeQuery(id+"F0.imprint","INTERSECT",VERTEX,{"derivedFrom":[sQuery(id+"F0.wireOp",EDGE,"E6.0"),subQ0]}),1.0]])],"derivedFrom":subQ0})])]})]}),makeQuery(id+"F4.opExtrude","SWEPT_FACE",FACE,{"disambiguationData":[OSD([sQuery(id+"F3.wireOp",EDGE,"E85.0")])]})]});}
            extrude(context, id + "F7", {"entities" : qUnion([Q0]), "operationType" : NewBodyOperationType.ADD, "endBound" : BoundingType.UP_TO_SURFACE, "oppositeDirection" : true, "depth" : 25 * mm, "endBoundEntityFace" : qUnion([Q1]), "offsetDistance" : 25 * mm});
        }
        {
            var Q0;
            {var subQ0=sQuery(id+"F0.wireOp",EDGE,"E6.1");Q0=makeQuery(id+"F7.boolean.opBoolean","MERGE",FACE,{"derivedFrom":[makeQuery(id+"F4.boolean.opBoolean","MERGE",FACE,{"derivedFrom":[makeQuery(id+"F2.boolean.opBoolean","MERGE",FACE,{"derivedFrom":[makeQuery(id+"F1.opExtrude","SWEPT_FACE",FACE,{"disambiguationData":[OSD([subQ0])]}),makeQuery(id+"F2.opExtrude","SWEPT_FACE",FACE,{"disambiguationData":[OSD([subQ0]),TDD([makeQuery(id+"F0.imprint","IMPRINT",EDGE,{"disambiguationData":[TD([[makeQuery(id+"F0.imprint","INTERSECT",VERTEX,{"derivedFrom":[subQ0,sQuery(id+"F0.wireOp",EDGE,"E6.2")]}),-1.0]])],"derivedFrom":subQ0})])]}),makeQuery(id+"F2.opExtrude","SWEPT_FACE",FACE,{"disambiguationData":[OSD([subQ0]),TDD([makeQuery(id+"F0.imprint","IMPRINT",EDGE,{"disambiguationData":[TD([[makeQuery(id+"F0.imprint","INTERSECT",VERTEX,{"derivedFrom":[sQuery(id+"F0.wireOp",EDGE,"E6.0"),subQ0]}),1.0]])],"derivedFrom":subQ0})])]})]}),makeQuery(id+"F4.opExtrude","SWEPT_FACE",FACE,{"disambiguationData":[OSD([sQuery(id+"F3.wireOp",EDGE,"E85.0")])]})]}),makeQuery(id+"F7.opExtrude","CAP_FACE",FACE,{"disambiguationData":[OSD([sQuery(id+"F5.wireOp",EDGE,"E91"),sQuery(id+"F5.wireOp",EDGE,"E92.MirrorCS"),sQuery(id+"F5.wireOp",EDGE,"E96"),sQuery(id+"F5.wireOp",EDGE,"E97"),sQuery(id+"F5.wireOp",EDGE,"E98"),sQuery(id+"F5.wireOp",EDGE,"E99.MirrorCS"),sQuery(id+"F5.wireOp",EDGE,"E100.MirrorCS"),sQuery(id+"F5.wireOp",EDGE,"E101.MirrorCS")])],"isStart":false})]});}
            extrude(context, id + "F8", {"entities" : qUnion([Q0]), "operationType" : NewBodyOperationType.ADD, "depth" : 70 * mm, "offsetDistance" : 25 * mm});
        }
    });
